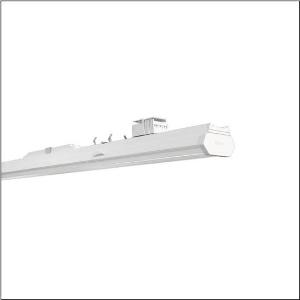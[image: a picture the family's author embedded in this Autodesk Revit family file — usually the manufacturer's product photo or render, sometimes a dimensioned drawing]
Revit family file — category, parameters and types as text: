
# Revit family: licross_r__21_protected_ho_52td11dn4axs_7332
name_source: partatom
category: Lighting Fixtures
units: mm (PartAtom-declared; Revit-internal decimal feet)

## family parameters
Cut with Voids When Loaded = No
Host = Face
Light Source = No
Part Type = Normal
Room Calculation Point = No
Round Connector Dimension = Use Diameter
Shared = No

## types (1)
- --- (1 x LED, 10000 lm, 55.1 W, 4000K)
    Apparent Load = 55 VA
    CIE Flux Codes = 84 94 98 99 100
    Color Rendering = 80
    Color Temperature = 4000K
    Default Elevation = 1800 mm
    Description = Licross® 21 Protected HO, luminaire insert, of sheet steel, galvanised, coil coated, white, length: 1.500mm, width: 90mm, height: 103mm, LED rated luminous flux: 10.000lm, light colour: 840, control gear: DALI 2, with plug, 5-pole, with phase selection, mains connection: 220..240V, AC, 50/60Hz, rated input power: 55W, halogen-free wiring, primary light control with lens, of plastic, primary optical cover: cover, of PMMA, light emission: direct distribution, primary light characteristic: symmetric, protection rating (complete): IP54, insulation class (complete): insulation class I (protective earthing), certification: CE, ENEC, VDE, UKCA, protection symbol: D if used in an environment with non-conductive dust loads with corresponding accessories, impact resistance: IK06, permissible ambient temperature for indoor applications: -25..+45°C, corresponds to IFS (International Featured Standards) requirements for safety and quality in the food industry, reducing of maximum allowable ambient temperature of 5°C with ceiling mounting, LABS conformity tested according to VDMA 24364:2018-05, packaging unit: 1 piece
    Height = 92 mm
    Lamp = 1 x LED
    Lamp Light Flux = 10000 lm
    Lamp Power = 55.1 W
    Lamp count = 1
    Length = 1500 mm
    Luminous efficacy = 181 lm/W
    Manufacturer = Siteco
    ModVariant = No
    Model = 52TD11DN4AXS
    Mounting Place = Ceiling
    Mounting Type = Pendant
    Number of Poles = 1
    OnlyDefault = Yes
    Power Factor = 1
    Product Name = Licross® 21 Protected HO
    Product group = luminaire insert
    ProductGroupID = 901
    Protection Class = Protection class I
    Protection Degree = IP 54
    RLX_Detail_Level = 1
    RLX_Emergency_Light_Flux = 0 lm
    RLX_Emergency_Type = 0
    RLX_Emergency_Type_DB = No
    RlxData = <blob elided: 24189 chars, md5=254777a9>
    Socket = socket
    Standby Power = 0 W
    System Light Flux = 10000 lm
    System Power = 55 W
    Type Comments = factory setting: luminous flux: 100 % | dim-lin: 254 | 316 mA
    Type Image = l_1256148.jpg
    URL = http://relux.com
    VarID = @adj_078201
    Voltage = 0 V
    Weight = 0.00 kg
    Width = 88 mm

## geometry (parser evidence)
native form markers: Blend x4, Sweep x10
no freeform markers — native parametric forms only
